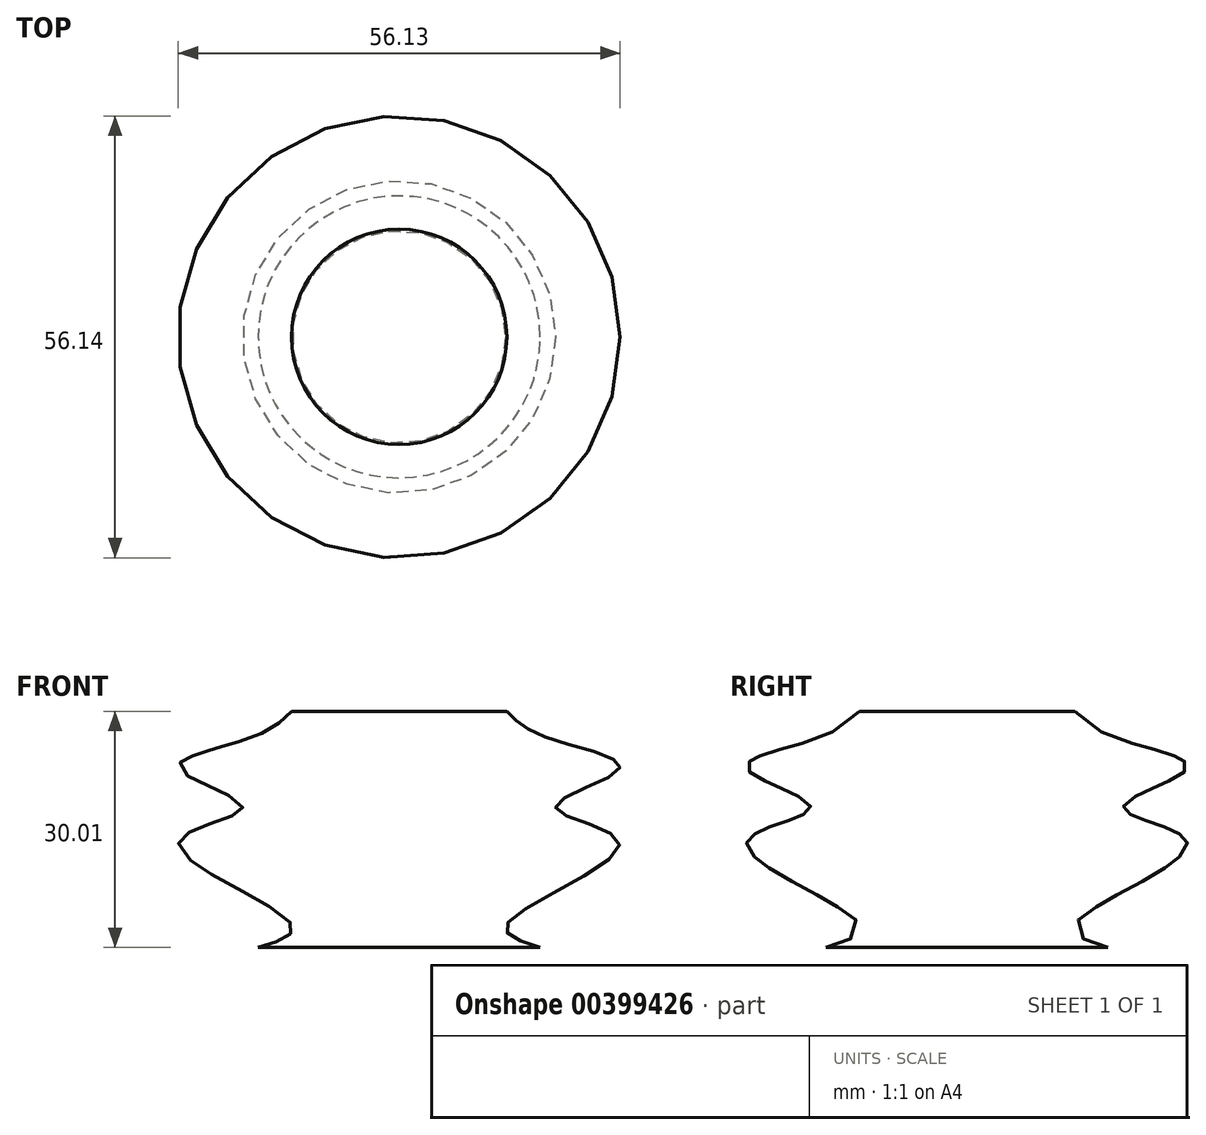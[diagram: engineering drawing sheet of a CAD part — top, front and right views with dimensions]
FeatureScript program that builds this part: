
annotation { "Feature Type Name" : "Feature", "Feature Type Description" : "" }
export const myFeature = defineFeature(function(context is Context, id is Id, definition is map)
    precondition{}
    {
        {
            var Q0;
            Q0=qCreatedBy(makeId("Front.planeOp"),FACE);
            var sketch = newSketch(context, id + "F0", { "sketchPlane" : qUnion([Q0])});
            skLineSegment(sketch, "E0", {"start": v(-50.3, 36.44) * mm, "end": v(-63.99, 36.44) * mm});
            skLineSegment(sketch, "E1", {"start": v(-63.99, 36.44) * mm, "end": v(-63.99, 6.43) * mm});
            skLineSegment(sketch, "E2", {"start": v(-63.99, 6.43) * mm, "end": v(-46.08, 6.43) * mm});
            skFitSpline(sketch, "E3", {"points": [v(-50.3, 36.44) * mm, v(-45.1, 33.06) * mm, v(-35.98, 29.18) * mm, v(-44.12, 24.22) * mm, v(-35.98, 19.73) * mm, v(-50.3, 9.41) * mm, v(-46.08, 6.43) * mm], "startDerivative": vector(25.88, -25.88) * mm, "endDerivative": vector(61.36, -18.66) * mm});
            skSolve(sketch);
        }
        {
            var Q0;
            Q0=makeQuery(id+"F0.imprint","IMPRINT",FACE,{"disambiguationData":[TD([[makeQuery(id+"F0.imprint","IMPRINT",EDGE,{"derivedFrom":sQuery(id+"F0.wireOp",EDGE,"E0")}),1.0]])]});
            var Q1;
            Q1=sQuery(id+"F0.wireOp",EDGE,"E1");
            revolve(context, id + "F1", {"entities" : qUnion([Q0]), "axis" : qUnion([Q1]), "revolveType" : RevolveType.FULL});
        }
    });
